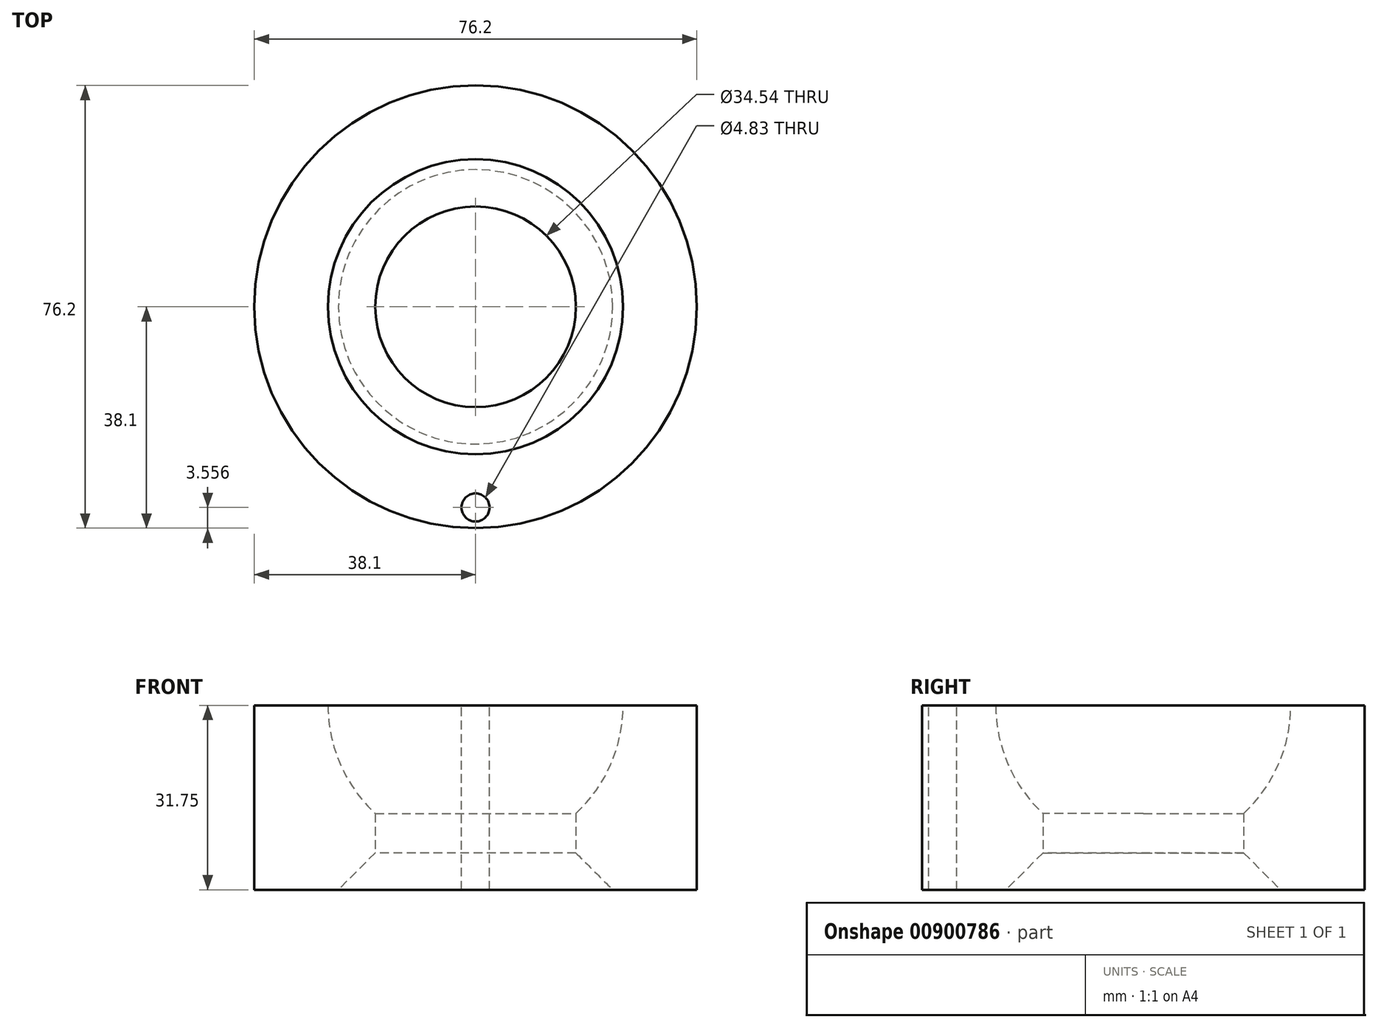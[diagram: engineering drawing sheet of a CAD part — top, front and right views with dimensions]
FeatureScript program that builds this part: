
annotation { "Feature Type Name" : "Feature", "Feature Type Description" : "" }
export const myFeature = defineFeature(function(context is Context, id is Id, definition is map)
    precondition{}
    {
        {
            var Q0;
            Q0=qCreatedBy(makeId("Front.planeOp"),FACE);
            var sketch = newSketch(context, id + "F0", { "sketchPlane" : qUnion([Q0])});
            skArc(sketch, "E0", {"start": v(-25.4, 0) * mm, "mid": v(-17.96, -17.96) * mm, "end": v(0, -25.4) * mm});
            skLineSegment(sketch, "E1", {"start": v(-25.4, 0) * mm, "end": v(-38.1, 0) * mm});
            skLineSegment(sketch, "E2", {"start": v(-38.1, 0) * mm, "end": v(-38.1, -31.75) * mm});
            skLineSegment(sketch, "E3", {"start": v(-38.1, -31.75) * mm, "end": v(0, -31.75) * mm});
            skLineSegment(sketch, "E4", {"start": v(0, -31.75) * mm, "end": v(0, -25.4) * mm});
            skSolve(sketch);
        }
        {
            var Q0;
            Q0=makeQuery(id+"F0.imprint","IMPRINT",FACE,{"disambiguationData":[TD([[makeQuery(id+"F0.imprint","IMPRINT",EDGE,{"derivedFrom":sQuery(id+"F0.wireOp",EDGE,"E0")}),-1.0]])]});
            var Q1;
            Q1=sQuery(id+"F0.wireOp",EDGE,"E4");
            revolve(context, id + "F1", {"surfaceOperationType" : NewSurfaceOperationType.NEW, "entities" : qUnion([Q0]), "axis" : qUnion([Q1]), "revolveType" : RevolveType.FULL});
        }
        {
            var Q0;
            Q0=qCreatedBy(makeId("Top.planeOp"),FACE);
            cPlane(context, id + "F2", {"entities" : qUnion([Q0]), "cplaneType" : CPlaneType.OFFSET, "offset" : 37.3 * mm, "oppositeDirection" : true, "width" : 152.4 * mm, "height" : 152.4 * mm});
        }
        {
            var Q0;
            Q0=qCreatedBy(id+"F2.planeOp",FACE);
            var sketch = newSketch(context, id + "F3", { "sketchPlane" : qUnion([Q0])});
            skCircle(sketch, "E5", {"center": v(0, 0) * mm, "radius": 17.27 * mm});
            skSolve(sketch);
        }
        {
            var Q0;
            Q0=makeQuery(id+"F3.imprint","IMPRINT",FACE,{"disambiguationData":[TD([[makeQuery(id+"F3.imprint","IMPRINT",EDGE,{"derivedFrom":sQuery(id+"F3.wireOp",EDGE,"E5")}),1.0]])]});
            extrude(context, id + "F4", {"entities" : qUnion([Q0]), "operationType" : NewBodyOperationType.REMOVE, "depth" : 25.4 * mm, "offsetDistance" : 25.4 * mm});
        }
        {
            var Q0;
            Q0=makeQuery(id+"F4.boolean.opBoolean","INTERSECT",EDGE,{"derivedFrom":[makeQuery(id+"F1.opRevolve","SWEPT_FACE",FACE,{"disambiguationData":[OSD([sQuery(id+"F0.wireOp",EDGE,"E3")])]}),makeQuery(id+"F4.opExtrude","SWEPT_FACE",FACE,{"disambiguationData":[OSD([sQuery(id+"F3.wireOp",EDGE,"E5")])]})]});
            chamfer(context, id + "F5", {"entities" : qUnion([Q0]), "width" : 6.35 * mm, "tangentPropagation" : true});
        }
        {
            var Q0;
            Q0=qCreatedBy(makeId("Top.planeOp"),FACE);
            var sketch = newSketch(context, id + "F6", { "sketchPlane" : qUnion([Q0])});
            skPoint(sketch, "E6", {"position": v(0, -34.54) * mm});
            skSolve(sketch);
        }
        {
            var Q0;
            Q0=sQuery(id+"F6.wireOp",VERTEX,"E6");
            var Q1;
            Q1=makeQuery(id+"F1.opRevolve","SWEPT_BODY",BODY,{"disambiguationData":[OSD([sQuery(id+"F0.wireOp",EDGE,"E0"),sQuery(id+"F0.wireOp",EDGE,"E1"),sQuery(id+"F0.wireOp",EDGE,"E2"),sQuery(id+"F0.wireOp",EDGE,"E3"),sQuery(id+"F0.wireOp",EDGE,"E4")])]});
            hole(context, id + "F7", {"style" : HoleStyle.SIMPLE, "endStyle" : HoleEndStyle.THROUGH, "holeDiameter" : 4.83 * mm, "majorDiameter" : 6.35 * mm, "isTappedThrough" : true, "tappedDepth" : 12.7 * mm, "tapClearance" : 3, "locations" : qUnion([Q0]), "scope" : qUnion([Q1])});
        }
    });
